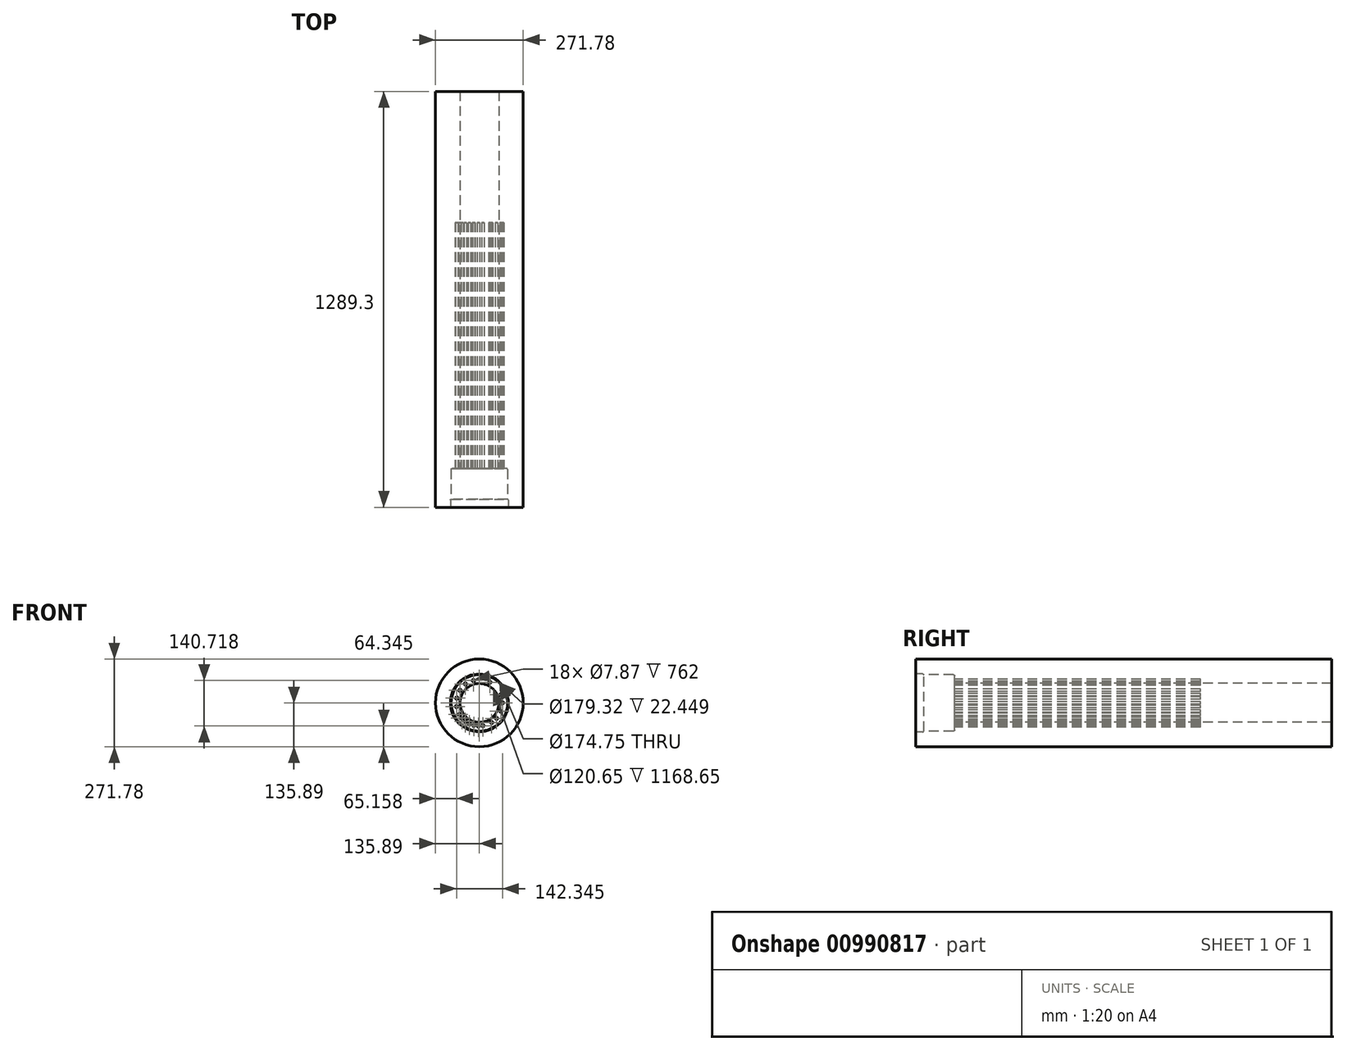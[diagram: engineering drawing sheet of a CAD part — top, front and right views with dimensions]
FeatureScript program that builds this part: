
annotation { "Feature Type Name" : "Feature", "Feature Type Description" : "" }
export const myFeature = defineFeature(function(context is Context, id is Id, definition is map)
    precondition{}
    {
        {
            var Q0;
            Q0=qCreatedBy(makeId("Front.planeOp"),FACE);
            var sketch = newSketch(context, id + "F0", { "sketchPlane" : qUnion([Q0])});
            skCircle(sketch, "E0", {"center": v(0, 0) * mm, "radius": 135.9 * mm});
            skSolve(sketch);
        }
        {
            var Q0;
            Q0=qSketchRegion(id+"F0",true);
            extrude(context, id + "F1", {"entities" : qUnion([Q0]), "depth" : 1289.3 * mm, "offsetDistance" : 25.4 * mm});
        }
        {
            var Q0;
            Q0=makeQuery(id+"F1.opExtrude","CAP_FACE",FACE,{"disambiguationData":[OSD([sQuery(id+"F0.wireOp",EDGE,"E0")])],"isStart":false});
            var sketch = newSketch(context, id + "F2", { "sketchPlane" : qUnion([Q0])});
            skCircle(sketch, "E1", {"center": v(0, 0) * mm, "radius": 87.38 * mm});
            skSolve(sketch);
        }
        {
            var Q0;
            Q0=qSketchRegion(id+"F2",true);
            extrude(context, id + "F3", {"entities" : qUnion([Q0]), "operationType" : NewBodyOperationType.REMOVE, "oppositeDirection" : true, "depth" : 120.65 * mm, "offsetDistance" : 25.4 * mm});
        }
        {
            var Q0;
            Q0=makeQuery(id+"F1.opExtrude","CAP_FACE",FACE,{"disambiguationData":[OSD([sQuery(id+"F0.wireOp",EDGE,"E0")])],"isStart":false});
            var sketch = newSketch(context, id + "F4", { "sketchPlane" : qUnion([Q0])});
            skCircle(sketch, "E2", {"center": v(0, 0) * mm, "radius": 89.66 * mm});
            skSolve(sketch);
        }
        {
            var Q0;
            Q0=qSketchRegion(id+"F4",true);
            extrude(context, id + "F5", {"entities" : qUnion([Q0]), "operationType" : NewBodyOperationType.REMOVE, "oppositeDirection" : true, "depth" : 25.4 * mm, "offsetDistance" : 25.4 * mm});
        }
        {
            var Q0;
            Q0=makeQuery(id+"F3.boolean.opBoolean","COPY",FACE,{"derivedFrom":makeQuery(id+"F3.opExtrude","CAP_FACE",FACE,{"disambiguationData":[OSD([sQuery(id+"F2.wireOp",EDGE,"E1")])],"isStart":false})});
            var sketch = newSketch(context, id + "F6", { "sketchPlane" : qUnion([Q0])});
            skCircle(sketch, "E3", {"center": v(0, 0) * mm, "radius": 60.33 * mm});
            skSolve(sketch);
        }
        {
            var Q0;
            Q0=qSketchRegion(id+"F6",true);
            extrude(context, id + "F7", {"entities" : qUnion([Q0]), "operationType" : NewBodyOperationType.REMOVE, "oppositeDirection" : true, "depth" : 1397 * mm, "offsetDistance" : 25.4 * mm});
        }
        {
            var Q0;
            Q0=makeQuery(id+"F3.boolean.opBoolean","COPY",EDGE,{"derivedFrom":makeQuery(id+"F3.opExtrude","CAP_EDGE",EDGE,{"disambiguationData":[OSD([sQuery(id+"F2.wireOp",EDGE,"E1")])],"isStart":false})});
            var Q1;
            Q1=makeQuery(id+"F5.boolean.opBoolean","COPY",EDGE,{"derivedFrom":makeQuery(id+"F5.opExtrude","CAP_EDGE",EDGE,{"disambiguationData":[OSD([sQuery(id+"F4.wireOp",EDGE,"E2")])],"isStart":false})});
            fillet(context, id + "F8", {"entities" : qUnion([Q0, Q1]), "radius" : 3.05 * mm, "tangentPropagation" : true, "allowEdgeOverflow" : false});
        }
        {
            var Q0;
            Q0=makeQuery(id+"F3.boolean.opBoolean","COPY",FACE,{"derivedFrom":makeQuery(id+"F3.opExtrude","CAP_FACE",FACE,{"disambiguationData":[OSD([sQuery(id+"F2.wireOp",EDGE,"E1")])],"isStart":false})});
            var sketch = newSketch(context, id + "F9", { "sketchPlane" : qUnion([Q0])});
            skPoint(sketch, "E4", {"position": v(71.61, 0) * mm});
            skPoint(sketch, "E5", {"position": v(32.51, 63.8) * mm});
            skPoint(sketch, "E6", {"position": v(-18.53, 69.17) * mm});
            skPoint(sketch, "E7", {"position": v(-43.1, 58.68) * mm});
            skPoint(sketch, "E8", {"position": v(-60.06, 39) * mm});
            skPoint(sketch, "E9", {"position": v(-70.05, 14.89) * mm});
            skPoint(sketch, "E10", {"position": v(66.86, -25.66) * mm});
            skPoint(sketch, "E11", {"position": v(66.86, 25.66) * mm});
            skPoint(sketch, "E12", {"position": v(53.22, -47.92) * mm});
            skPoint(sketch, "E13", {"position": v(37.95, -60.73) * mm});
            skPoint(sketch, "E14", {"position": v(11.2, -70.73) * mm});
            skPoint(sketch, "E15", {"position": v(-3.12, -71.55) * mm});
            skPoint(sketch, "E16", {"position": v(-17.32, -69.49) * mm});
            skPoint(sketch, "E17", {"position": v(-30.83, -64.64) * mm});
            skPoint(sketch, "E18", {"position": v(-43.1, -57.2) * mm});
            skPoint(sketch, "E19", {"position": v(-53.64, -47.45) * mm});
            skPoint(sketch, "E20", {"position": v(-62.02, -35.8) * mm});
            skPoint(sketch, "E21", {"position": v(-70.73, -11.2) * mm});
            skCircle(sketch, "E22", {"center": v(-60.06, 39) * mm, "radius": 3.94 * mm});
            skCircle(sketch, "E23", {"center": v(-43.1, 58.68) * mm, "radius": 3.94 * mm});
            skCircle(sketch, "E24", {"center": v(-18.53, 69.17) * mm, "radius": 3.94 * mm});
            skCircle(sketch, "E25", {"center": v(-70.05, 14.89) * mm, "radius": 3.94 * mm});
            skCircle(sketch, "E26", {"center": v(-70.73, -11.2) * mm, "radius": 3.94 * mm});
            skCircle(sketch, "E27", {"center": v(-62.02, -35.8) * mm, "radius": 3.94 * mm});
            skCircle(sketch, "E28", {"center": v(-53.64, -47.45) * mm, "radius": 3.94 * mm});
            skCircle(sketch, "E29", {"center": v(-43.1, -57.2) * mm, "radius": 3.94 * mm});
            skCircle(sketch, "E30", {"center": v(-30.83, -64.64) * mm, "radius": 3.94 * mm});
            skCircle(sketch, "E31", {"center": v(-17.32, -69.49) * mm, "radius": 3.94 * mm});
            skCircle(sketch, "E32", {"center": v(-3.12, -71.55) * mm, "radius": 3.94 * mm});
            skCircle(sketch, "E33", {"center": v(11.2, -70.73) * mm, "radius": 3.94 * mm});
            skCircle(sketch, "E34", {"center": v(37.95, -60.73) * mm, "radius": 3.94 * mm});
            skCircle(sketch, "E35", {"center": v(53.22, -47.92) * mm, "radius": 3.94 * mm});
            skCircle(sketch, "E36", {"center": v(66.86, -25.66) * mm, "radius": 3.94 * mm});
            skCircle(sketch, "E37", {"center": v(71.61, 0) * mm, "radius": 3.94 * mm});
            skCircle(sketch, "E38", {"center": v(66.86, 25.66) * mm, "radius": 3.94 * mm});
            skCircle(sketch, "E39", {"center": v(32.51, 63.8) * mm, "radius": 3.94 * mm});
            skSolve(sketch);
        }
        {
            var Q0;
            Q0=qSketchRegion(id+"F9",true);
            extrude(context, id + "F10", {"entities" : qUnion([Q0]), "operationType" : NewBodyOperationType.REMOVE, "oppositeDirection" : true, "depth" : 762 * mm, "offsetDistance" : 25.4 * mm});
        }
        {
            var Q0;
            Q0=qSketchRegion(id+"F9",true);
            extrude(context, id + "F11", {"entities" : qUnion([Q0]), "operationType" : NewBodyOperationType.REMOVE, "oppositeDirection" : true, "depth" : 762 * mm, "offsetDistance" : 25.4 * mm});
        }
    });
